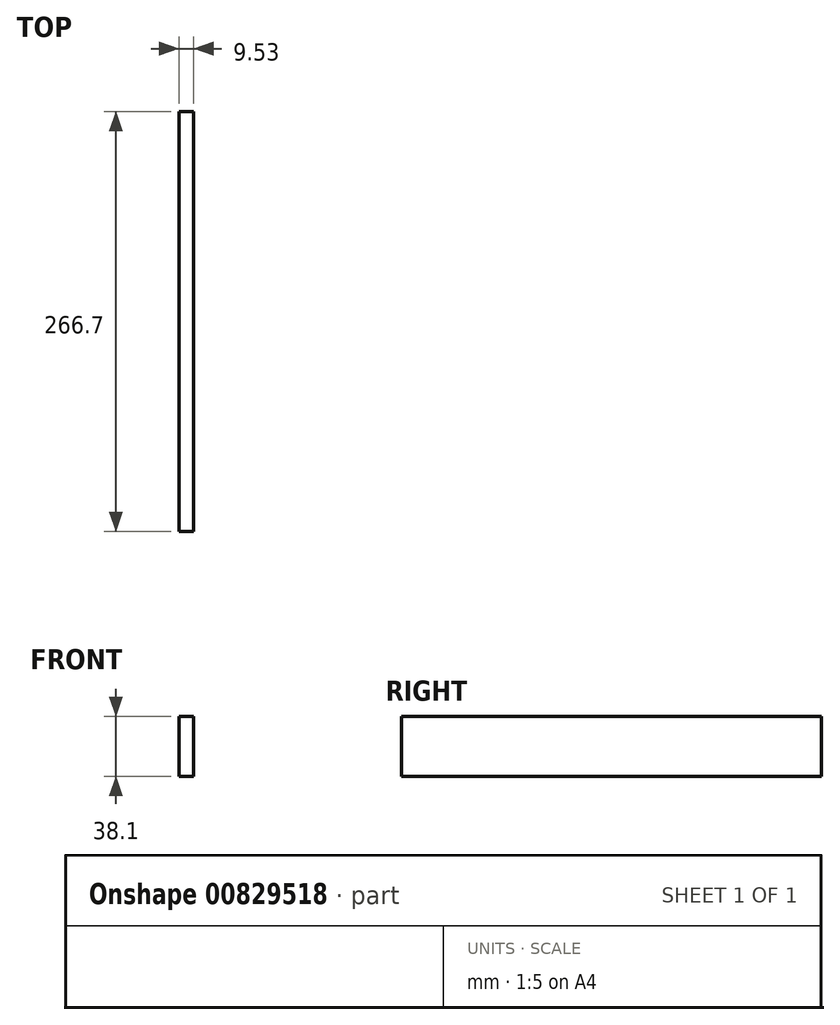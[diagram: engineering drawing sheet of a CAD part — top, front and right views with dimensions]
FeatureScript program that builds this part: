
annotation { "Feature Type Name" : "Feature", "Feature Type Description" : "" }
export const myFeature = defineFeature(function(context is Context, id is Id, definition is map)
    precondition{}
    {
        {
            var Q0;
            Q0=qCreatedBy(makeId("Right.planeOp"),FACE);
            var sketch = newSketch(context, id + "F0", { "sketchPlane" : qUnion([Q0])});
            skLineSegment(sketch, "E0.bottom", {"start": v(-133.35, -19.05) * mm, "end": v(133.35, -19.05) * mm});
            skLineSegment(sketch, "E0.top", {"start": v(-133.35, 19.05) * mm, "end": v(133.35, 19.05) * mm});
            skLineSegment(sketch, "E0.left", {"start": v(-133.35, -19.05) * mm, "end": v(-133.35, 19.05) * mm});
            skLineSegment(sketch, "E0.right", {"start": v(133.35, -19.05) * mm, "end": v(133.35, 19.05) * mm});
            skPoint(sketch, "E0.middle", {"position": v(0, 0) * mm});
            skSolve(sketch);
        }
        {
            var Q0;
            Q0=qSketchRegion(id+"F0",true);
            extrude(context, id + "F1", {"entities" : qUnion([Q0]), "depth" : 9.52 * mm, "offsetDistance" : 25.4 * mm});
        }
    });
